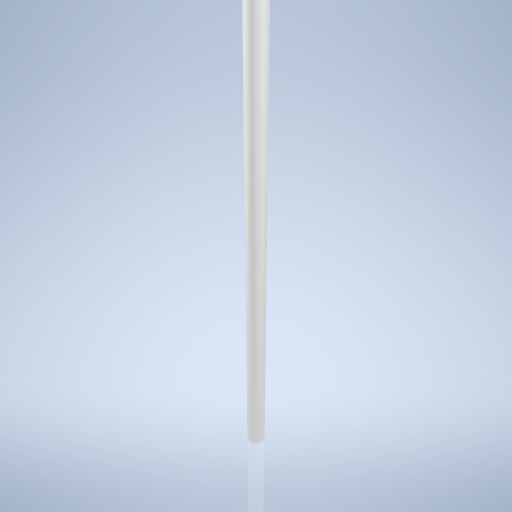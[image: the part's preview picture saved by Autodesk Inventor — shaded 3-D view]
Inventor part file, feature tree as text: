
AUTODESK INVENTOR PART (.ipt)
format: ipt  version: 2024.2 (Build 282272000, 272)  size: 235,008 bytes
history: native  units: mm
features: extrude x1, sketch x1
ambient origin geometry x8: Origin, YZ Plane, XZ Plane, XY Plane, X Axis, Y Axis, Z Axis, Center Point
bodies: Volumenkörper1 (feature_tree)
feature tree (2):
  extrude  "Extrusion1"  Depth=38.0mm TaperAngle=0.0deg
  sketch  "Skizze1"  dims[d0=1.5mm d1=38.0mm d2=0.0mm]
